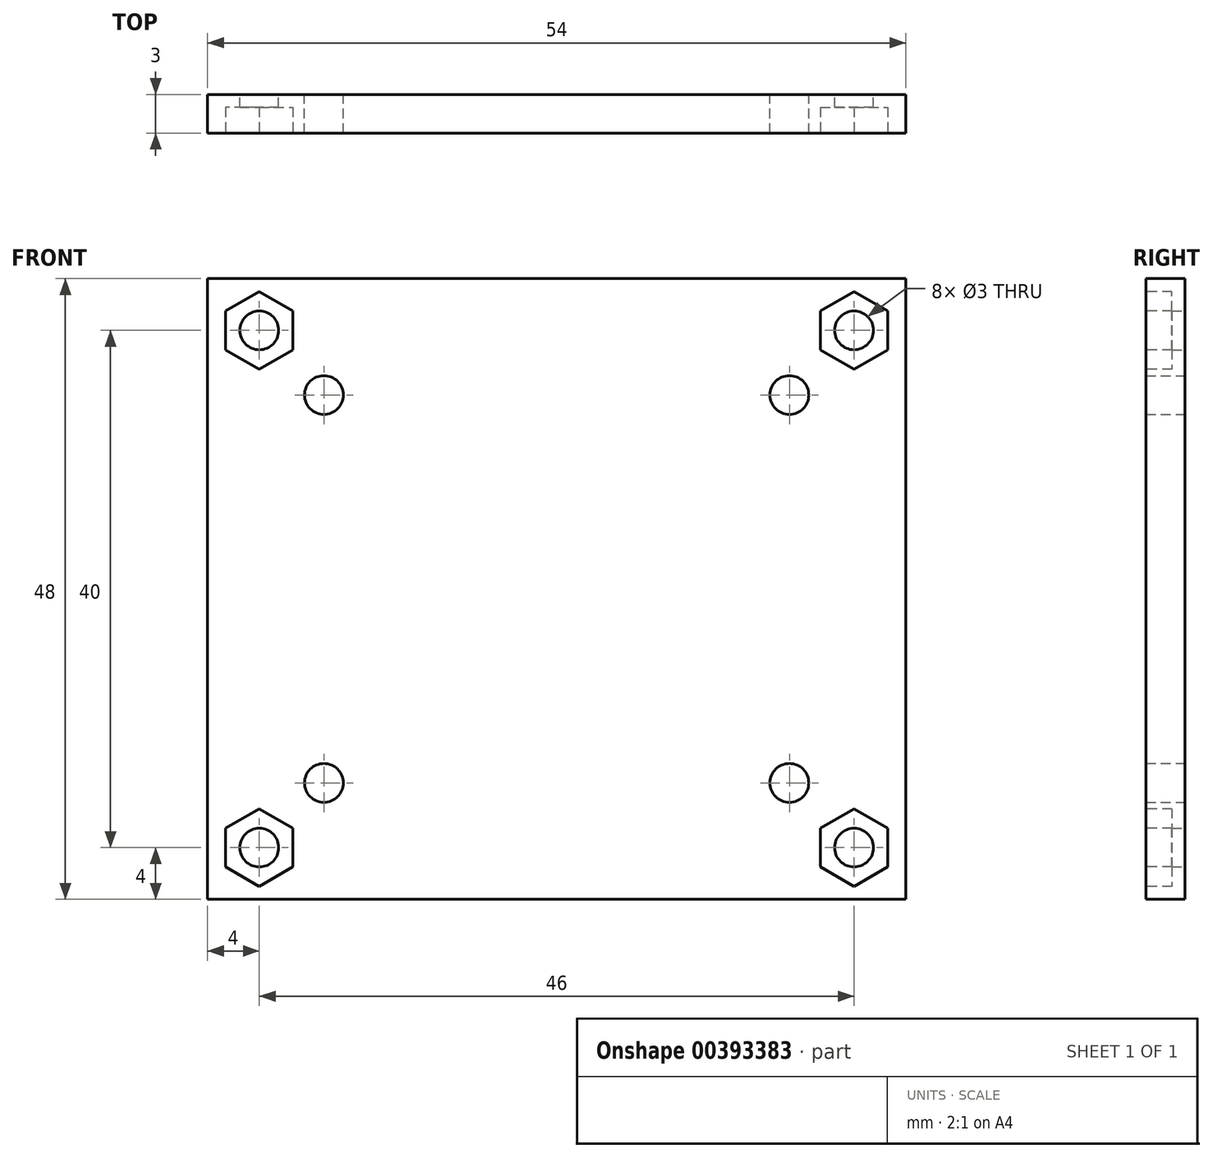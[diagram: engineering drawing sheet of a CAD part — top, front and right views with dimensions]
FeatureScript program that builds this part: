
annotation { "Feature Type Name" : "Feature", "Feature Type Description" : "" }
export const myFeature = defineFeature(function(context is Context, id is Id, definition is map)
    precondition{}
    {
        {
            var Q0;
            Q0=qCreatedBy(makeId("Front.planeOp"),FACE);
            var sketch = newSketch(context, id + "F0", { "sketchPlane" : qUnion([Q0])});
            skLineSegment(sketch, "E0.bottom", {"start": v(-27, 24) * mm, "end": v(27, 24) * mm});
            skLineSegment(sketch, "E0.top", {"start": v(-27, -24) * mm, "end": v(27, -24) * mm});
            skLineSegment(sketch, "E0.left", {"start": v(-27, 24) * mm, "end": v(-27, -24) * mm});
            skLineSegment(sketch, "E0.right", {"start": v(27, 24) * mm, "end": v(27, -24) * mm});
            skPoint(sketch, "E0.middle", {"position": v(0, 0) * mm});
            skCircle(sketch, "E1", {"center": v(-23, 20) * mm, "radius": 1.5 * mm});
            skCircle(sketch, "E2", {"center": v(-18, 15) * mm, "radius": 1.5 * mm});
            skCircle(sketch, "E3.MirrorC", {"center": v(23, 20) * mm, "radius": 1.5 * mm});
            skCircle(sketch, "E4.MirrorC", {"center": v(18, 15) * mm, "radius": 1.5 * mm});
            skCircle(sketch, "E5.MirrorC", {"center": v(-23, -20) * mm, "radius": 1.5 * mm});
            skLineSegment(sketch, "E6.MirrorCS", {"start": v(-27, -24) * mm, "end": v(-27, 24) * mm});
            skLineSegment(sketch, "E7.MirrorCS", {"start": v(27, -24) * mm, "end": v(27, 24) * mm});
            skCircle(sketch, "E8.MirrorC", {"center": v(18, -15) * mm, "radius": 1.5 * mm});
            skCircle(sketch, "E9.MirrorC", {"center": v(23, -20) * mm, "radius": 1.5 * mm});
            skCircle(sketch, "E10.MirrorC", {"center": v(-18, -15) * mm, "radius": 1.5 * mm});
            skSolve(sketch);
        }
        {
            var Q0;
            Q0=makeQuery(id+"F0.imprint","IMPRINT",FACE,{"disambiguationData":[TD([[makeQuery(id+"F0.imprint","IMPRINT",EDGE,{"derivedFrom":sQuery(id+"F0.wireOp",EDGE,"E0.bottom")}),-1.0]])]});
            extrude(context, id + "F1", {"entities" : qUnion([Q0]), "depth" : 3 * mm});
        }
        {
            var Q0;
            Q0=makeQuery(id+"F1.opExtrude","CAP_FACE",FACE,{"disambiguationData":[OSD([sQuery(id+"F0.wireOp",EDGE,"E0.bottom"),sQuery(id+"F0.wireOp",EDGE,"E0.top"),sQuery(id+"F0.wireOp",EDGE,"E4.MirrorC"),sQuery(id+"F0.wireOp",EDGE,"E2"),sQuery(id+"F0.wireOp",EDGE,"E3.MirrorC"),sQuery(id+"F0.wireOp",EDGE,"E1"),sQuery(id+"F0.wireOp",EDGE,"E9.MirrorC"),sQuery(id+"F0.wireOp",EDGE,"E6.MirrorCS"),sQuery(id+"F0.wireOp",EDGE,"E7.MirrorCS"),sQuery(id+"F0.wireOp",EDGE,"E5.MirrorC"),sQuery(id+"F0.wireOp",EDGE,"E8.MirrorC"),sQuery(id+"F0.wireOp",EDGE,"E10.MirrorC")])],"isStart":false});
            var sketch = newSketch(context, id + "F2", { "sketchPlane" : qUnion([Q0])});
            skCircle(sketch, "E11.cCircle", {"center": v(-23, 20) * mm, "radius": 2.6 * mm, "construction": true});
            skLineSegment(sketch, "E11.0", {"start": v(-25.6, 18.5) * mm, "end": v(-25.6, 21.5) * mm});
            skLineSegment(sketch, "E11.1", {"start": v(-25.6, 21.5) * mm, "end": v(-23, 23) * mm});
            skLineSegment(sketch, "E11.2", {"start": v(-23, 23) * mm, "end": v(-20.4, 21.5) * mm});
            skLineSegment(sketch, "E11.3", {"start": v(-20.4, 21.5) * mm, "end": v(-20.4, 18.5) * mm});
            skLineSegment(sketch, "E11.4", {"start": v(-20.4, 18.5) * mm, "end": v(-23, 17) * mm});
            skLineSegment(sketch, "E11.5", {"start": v(-23, 17) * mm, "end": v(-25.6, 18.5) * mm});
            skPoint(sketch, "E11.0.midPoint", {"position": v(-25.6, 20) * mm});
            skLineSegment(sketch, "E12.MirrorCS", {"start": v(23, 17) * mm, "end": v(25.6, 18.5) * mm});
            skLineSegment(sketch, "E13.MirrorCS", {"start": v(25.6, 21.5) * mm, "end": v(23, 23) * mm});
            skLineSegment(sketch, "E14.MirrorCS", {"start": v(20.4, 18.5) * mm, "end": v(23, 17) * mm});
            skLineSegment(sketch, "E15.MirrorCS", {"start": v(20.4, 21.5) * mm, "end": v(20.4, 18.5) * mm});
            skLineSegment(sketch, "E16.MirrorCS", {"start": v(23, 23) * mm, "end": v(20.4, 21.5) * mm});
            skLineSegment(sketch, "E17.MirrorCS", {"start": v(25.6, 18.5) * mm, "end": v(25.6, 21.5) * mm});
            skCircle(sketch, "E18.MirrorC", {"center": v(23, 20) * mm, "radius": 2.6 * mm, "construction": true});
            skPoint(sketch, "E19.MirrorP", {"position": v(25.6, 20) * mm});
            skLineSegment(sketch, "E20.MirrorCS", {"start": v(20.4, -18.5) * mm, "end": v(23, -17) * mm});
            skLineSegment(sketch, "E21.MirrorCS", {"start": v(23, -23) * mm, "end": v(20.4, -21.5) * mm});
            skLineSegment(sketch, "E22.MirrorCS", {"start": v(-25.6, -21.5) * mm, "end": v(-23, -23) * mm});
            skLineSegment(sketch, "E23.MirrorCS", {"start": v(-23, -17) * mm, "end": v(-25.6, -18.5) * mm});
            skLineSegment(sketch, "E24.MirrorCS", {"start": v(-23, -23) * mm, "end": v(-20.4, -21.5) * mm});
            skLineSegment(sketch, "E25.MirrorCS", {"start": v(23, -17) * mm, "end": v(25.6, -18.5) * mm});
            skLineSegment(sketch, "E26.MirrorCS", {"start": v(25.6, -21.5) * mm, "end": v(23, -23) * mm});
            skLineSegment(sketch, "E27.MirrorCS", {"start": v(20.4, -21.5) * mm, "end": v(20.4, -18.5) * mm});
            skLineSegment(sketch, "E28.MirrorCS", {"start": v(-25.6, -18.5) * mm, "end": v(-25.6, -21.5) * mm});
            skLineSegment(sketch, "E29.MirrorCS", {"start": v(25.6, -18.5) * mm, "end": v(25.6, -21.5) * mm});
            skLineSegment(sketch, "E30.MirrorCS", {"start": v(-20.4, -21.5) * mm, "end": v(-20.4, -18.5) * mm});
            skLineSegment(sketch, "E31.MirrorCS", {"start": v(-20.4, -18.5) * mm, "end": v(-23, -17) * mm});
            skCircle(sketch, "E32.MirrorC", {"center": v(-23, -20) * mm, "radius": 2.6 * mm, "construction": true});
            skCircle(sketch, "E33.MirrorC", {"center": v(23, -20) * mm, "radius": 2.6 * mm, "construction": true});
            skPoint(sketch, "E34.MirrorP", {"position": v(25.6, -20) * mm});
            skPoint(sketch, "E35.MirrorP", {"position": v(-25.6, -20) * mm});
            skSolve(sketch);
        }
        {
            var Q0;
            Q0=makeQuery(id+"F2.imprint","IMPRINT",FACE,{"disambiguationData":[TD([[makeQuery(id+"F2.imprint","IMPRINT",EDGE,{"derivedFrom":sQuery(id+"F2.wireOp",EDGE,"E23.MirrorCS")}),1.0]])]});
            var Q1;
            Q1=makeQuery(id+"F2.imprint","IMPRINT",FACE,{"disambiguationData":[TD([[makeQuery(id+"F2.imprint","IMPRINT",EDGE,{"derivedFrom":sQuery(id+"F2.wireOp",EDGE,"E21.MirrorCS")}),-1.0]])]});
            var Q2;
            Q2=makeQuery(id+"F2.imprint","IMPRINT",FACE,{"disambiguationData":[TD([[makeQuery(id+"F2.imprint","IMPRINT",EDGE,{"derivedFrom":sQuery(id+"F2.wireOp",EDGE,"E11.4")}),-1.0]])]});
            var Q3;
            Q3=makeQuery(id+"F2.imprint","IMPRINT",FACE,{"disambiguationData":[TD([[makeQuery(id+"F2.imprint","IMPRINT",EDGE,{"derivedFrom":sQuery(id+"F2.wireOp",EDGE,"E12.MirrorCS")}),1.0]])]});
            extrude(context, id + "F3", {"entities" : qUnion([Q0, Q1, Q2, Q3]), "operationType" : NewBodyOperationType.REMOVE, "oppositeDirection" : true, "depth" : 2 * mm});
        }
    });
